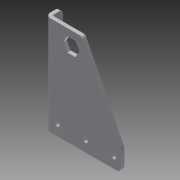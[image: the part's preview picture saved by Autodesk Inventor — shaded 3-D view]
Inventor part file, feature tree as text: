
AUTODESK INVENTOR PART (.ipt)
format: ipt  version: 2014 (Build 180170000, 170)  size: 185,856 bytes
history: native  units: in
note: dims shown in document units (in); Inventor stores cm internally (conversion verified against a paired STEP export)
features: sheet_metal_op x4, other x4, sketch x2, fillet x1
ambient origin geometry x8: Origin, YZ Plane, XZ Plane, XY Plane, X Axis, Y Axis, Z Axis, Center Point
bodies: Solid1 (feature_tree)
feature tree (11):
  sheet_metal_op  "Face1"
  sheet_metal_op  "Flange2"
  fillet  "Fillet1"  Radius=0.125in
  sketch  "Sketch1"  dims[d5=2.5in d6=0.163in d7=0.25in d8=0.375in d11=0.125in]
  other  "Plate1"
  sketch  "Sketch3"  dims[d22=1.1811in d24=1.0in d25=0.3937in d27=1.0in d29=3.5in d30=0.75in d31=1.125in d32=0.5in d34=0.75in d35=0.5in d36=0.125in d37=0.0625in d38=0.25in d39=0.125in d40=0.5in d41=90.0deg d42=0.05in d43=0.5in d44=0.125in d45=0.125in d46=0.125in d0=0.125in d1=0.125in d2=0.125in d3=0.0in]
  other  "Plate3"
  sheet_metal_op  "Bend2"
  sheet_metal_op  "Corner2"
  other  "Definition1"
  other  "Cut1"
